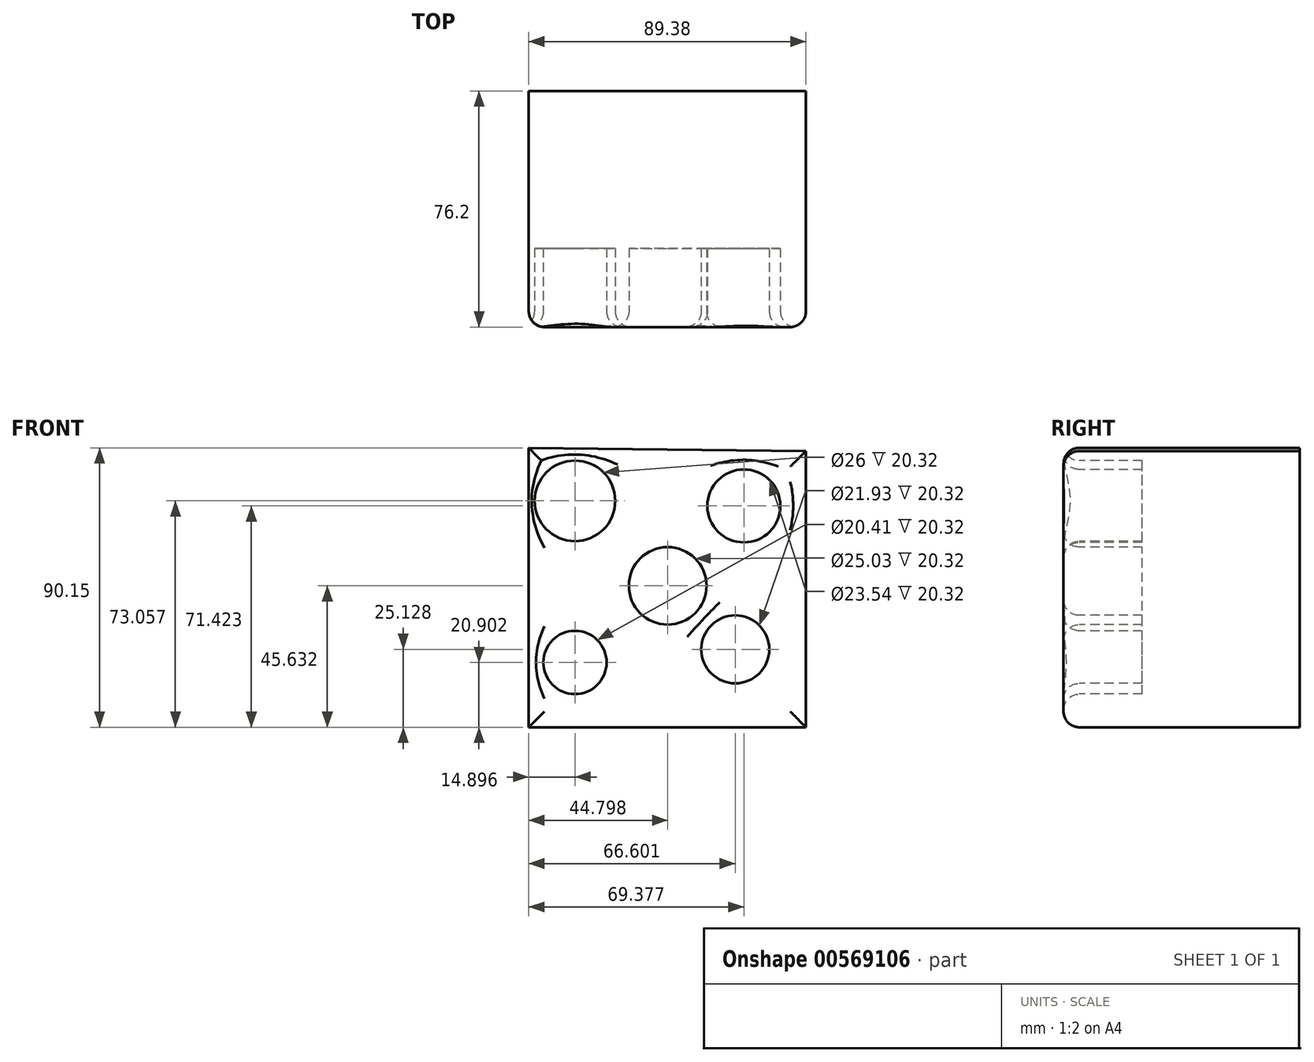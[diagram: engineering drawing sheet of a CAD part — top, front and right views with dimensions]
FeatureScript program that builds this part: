
annotation { "Feature Type Name" : "Feature", "Feature Type Description" : "" }
export const myFeature = defineFeature(function(context is Context, id is Id, definition is map)
    precondition{}
    {
        {
            var Q0;
            Q0=qCreatedBy(makeId("Front.planeOp"),FACE);
            var sketch = newSketch(context, id + "F0", { "sketchPlane" : qUnion([Q0])});
            skLineSegment(sketch, "E0", {"start": v(-33.13, 49.7) * mm, "end": v(-33.13, -40.45) * mm});
            skLineSegment(sketch, "E1", {"start": v(-33.13, -40.45) * mm, "end": v(56.25, -40.45) * mm});
            skLineSegment(sketch, "E2", {"start": v(56.25, -40.45) * mm, "end": v(56.25, 48.67) * mm});
            skLineSegment(sketch, "E3", {"start": v(56.25, 48.67) * mm, "end": v(-33.13, 49.7) * mm});
            skSolve(sketch);
        }
        {
            var Q0;
            Q0 = qSketchRegion(id + "F0", true);
            extrude(context, id + "F1", {"entities" : qUnion([Q0]), "depth" : 76.2 * mm, "offsetDistance" : 25.4 * mm});
        }
        {
            var Q0;
            Q0=makeQuery(id+"F1.opExtrude","CAP_FACE",FACE,{"disambiguationData":[OSD([sQuery(id+"F0.wireOp",EDGE,"E0"),sQuery(id+"F0.wireOp",EDGE,"E1"),sQuery(id+"F0.wireOp",EDGE,"E2"),sQuery(id+"F0.wireOp",EDGE,"E3")])],"isStart":false});
            var sketch = newSketch(context, id + "F2", { "sketchPlane" : qUnion([Q0])});
            skCircle(sketch, "E4", {"center": v(11.67, 5.18) * mm, "radius": 12.51 * mm});
            skCircle(sketch, "E5", {"center": v(36.25, 30.97) * mm, "radius": 11.77 * mm});
            skCircle(sketch, "E6", {"center": v(33.47, -15.32) * mm, "radius": 10.96 * mm});
            skCircle(sketch, "E7", {"center": v(-18.23, -19.55) * mm, "radius": 10.2 * mm});
            skCircle(sketch, "E8", {"center": v(-18.23, 32.6) * mm, "radius": 13 * mm});
            skSolve(sketch);
        }
        {
            var Q0;
            Q0=makeQuery(id+"F2.imprint","IMPRINT",FACE,{"disambiguationData":[TD([[makeQuery(id+"F2.imprint","IMPRINT",EDGE,{"derivedFrom":sQuery(id+"F2.wireOp",EDGE,"E4")}),-1.0]])]});
            var sketch = newSketch(context, id + "F3", { "sketchPlane" : qUnion([Q0])});
            skSolve(sketch);
        }
        {
            var Q0;
            Q0 = qSketchRegion(id + "F3", true);
            var Q1;
            Q1=makeQuery(id+"F2.imprint","IMPRINT",FACE,{"disambiguationData":[TD([[makeQuery(id+"F2.imprint","IMPRINT",EDGE,{"derivedFrom":sQuery(id+"F2.wireOp",EDGE,"E8")}),1.0]])]});
            var Q2;
            Q2=makeQuery(id+"F2.imprint","IMPRINT",FACE,{"disambiguationData":[TD([[makeQuery(id+"F2.imprint","IMPRINT",EDGE,{"derivedFrom":sQuery(id+"F2.wireOp",EDGE,"E5")}),1.0]])]});
            var Q3;
            Q3=makeQuery(id+"F2.imprint","IMPRINT",FACE,{"disambiguationData":[TD([[makeQuery(id+"F2.imprint","IMPRINT",EDGE,{"derivedFrom":sQuery(id+"F2.wireOp",EDGE,"E4")}),1.0]])]});
            var Q4;
            Q4=makeQuery(id+"F2.imprint","IMPRINT",FACE,{"disambiguationData":[TD([[makeQuery(id+"F2.imprint","IMPRINT",EDGE,{"derivedFrom":sQuery(id+"F2.wireOp",EDGE,"E7")}),1.0]])]});
            var Q5;
            Q5=makeQuery(id+"F2.imprint","IMPRINT",FACE,{"disambiguationData":[TD([[makeQuery(id+"F2.imprint","IMPRINT",EDGE,{"derivedFrom":sQuery(id+"F2.wireOp",EDGE,"E6")}),1.0]])]});
            extrude(context, id + "F4", {"entities" : qUnion([Q0, Q1, Q2, Q3, Q4, Q5]), "operationType" : NewBodyOperationType.REMOVE, "oppositeDirection" : true, "depth" : 25.4 * mm, "offsetDistance" : 25.4 * mm});
        }
        {
            var Q0;
            Q0=makeQuery(id+"F1.opExtrude","CAP_FACE",FACE,{"disambiguationData":[OSD([sQuery(id+"F0.wireOp",EDGE,"E0"),sQuery(id+"F0.wireOp",EDGE,"E1"),sQuery(id+"F0.wireOp",EDGE,"E2"),sQuery(id+"F0.wireOp",EDGE,"E3")])],"isStart":false});
            var Q1;
            Q1=makeQuery(id+"F1.opExtrude","CAP_EDGE",EDGE,{"disambiguationData":[OSD([sQuery(id+"F0.wireOp",EDGE,"E0")])],"isStart":false});
            fillet(context, id + "F5", {"entities" : qUnion([Q0, Q1]), "radius" : 5.08 * mm, "tangentPropagation" : true, "allowEdgeOverflow" : false});
        }
    });
